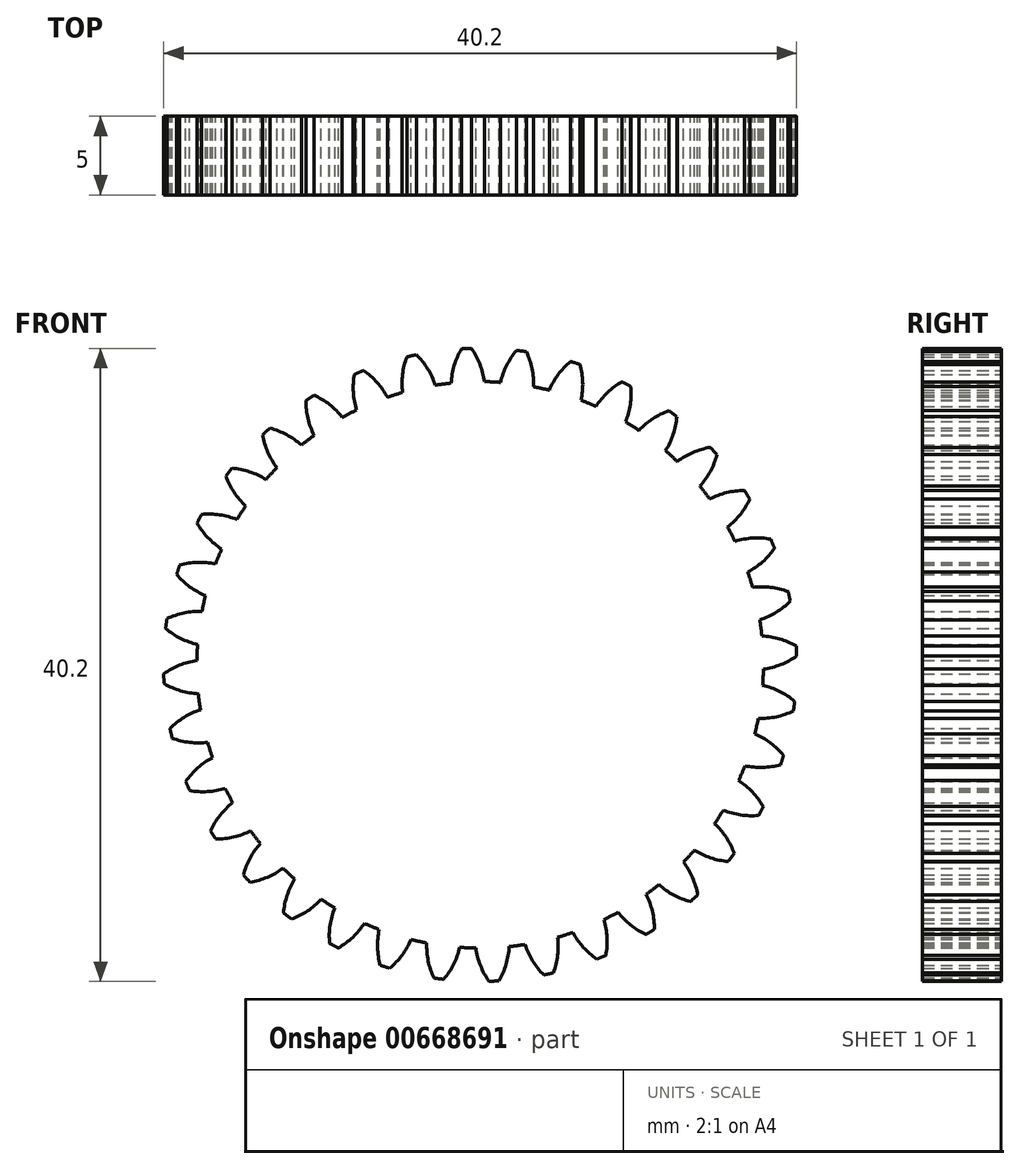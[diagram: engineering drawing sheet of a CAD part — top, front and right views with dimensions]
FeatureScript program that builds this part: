
annotation { "Feature Type Name" : "Feature", "Feature Type Description" : "" }
export const myFeature = defineFeature(function(context is Context, id is Id, definition is map)
    precondition{}
    {
        {
            var Q0;
            Q0=qCreatedBy(makeId("Front.planeOp"),FACE);
            var sketch = newSketch(context, id + "F0", { "sketchPlane" : qUnion([Q0])});
            skLineSegment(sketch, "E0", {"start": v(0, 0) * mm, "end": v(-1.18, 26.95) * mm, "construction": true});
            skArc(sketch, "E1.trimOffspring", {"start": v(0.27, 17.99) * mm, "mid": v(-0.02, 19.1) * mm, "end": v(-0.56, 20.1) * mm});
            skArc(sketch, "E2", {"start": v(-0.56, 20.1) * mm, "mid": v(-0.72, 20.1) * mm, "end": v(-0.88, 20.09) * mm});
            skArc(sketch, "E3.MirrorCS", {"start": v(-1.2, 20.07) * mm, "mid": v(-1.03, 20.08) * mm, "end": v(-0.88, 20.09) * mm});
            skArc(sketch, "E4.MirrorCS", {"start": v(-1.84, 17.9) * mm, "mid": v(-1.65, 19.02) * mm, "end": v(-1.2, 20.07) * mm});
            skArc(sketch, "E5.1.0", {"start": v(-2.85, 17.76) * mm, "mid": v(-3.33, 18.8) * mm, "end": v(-4.05, 19.7) * mm});
            skArc(sketch, "E5.1.1", {"start": v(-4.05, 19.7) * mm, "mid": v(-4.2, 19.66) * mm, "end": v(-4.35, 19.63) * mm});
            skArc(sketch, "E5.1.2", {"start": v(-4.92, 17.3) * mm, "mid": v(-4.93, 18.45) * mm, "end": v(-4.66, 19.56) * mm});
            skArc(sketch, "E5.1.3", {"start": v(-4.66, 19.56) * mm, "mid": v(-4.5, 19.6) * mm, "end": v(-4.35, 19.63) * mm});
            skArc(sketch, "E5.2.0", {"start": v(-5.9, 17) * mm, "mid": v(-6.55, 17.94) * mm, "end": v(-7.4, 18.7) * mm});
            skArc(sketch, "E5.2.1", {"start": v(-7.4, 18.7) * mm, "mid": v(-7.55, 18.64) * mm, "end": v(-7.7, 18.58) * mm});
            skArc(sketch, "E5.2.2", {"start": v(-7.85, 16.19) * mm, "mid": v(-8.05, 17.31) * mm, "end": v(-7.98, 18.46) * mm});
            skArc(sketch, "E5.2.3", {"start": v(-7.98, 18.46) * mm, "mid": v(-7.84, 18.52) * mm, "end": v(-7.7, 18.58) * mm});
            skArc(sketch, "E5.3.0", {"start": v(-8.76, 15.71) * mm, "mid": v(-9.56, 16.53) * mm, "end": v(-10.54, 17.13) * mm});
            skArc(sketch, "E5.3.1", {"start": v(-10.54, 17.13) * mm, "mid": v(-10.67, 17.04) * mm, "end": v(-10.8, 16.96) * mm});
            skArc(sketch, "E5.3.2", {"start": v(-10.54, 14.58) * mm, "mid": v(-10.94, 15.65) * mm, "end": v(-11.07, 16.79) * mm});
            skArc(sketch, "E5.3.3", {"start": v(-11.07, 16.79) * mm, "mid": v(-10.94, 16.87) * mm, "end": v(-10.8, 16.96) * mm});
            skArc(sketch, "E5.4.0", {"start": v(-11.35, 13.96) * mm, "mid": v(-12.29, 14.62) * mm, "end": v(-13.35, 15.04) * mm});
            skArc(sketch, "E5.4.1", {"start": v(-13.35, 15.04) * mm, "mid": v(-13.47, 14.93) * mm, "end": v(-13.58, 14.83) * mm});
            skArc(sketch, "E5.4.2", {"start": v(-12.91, 12.53) * mm, "mid": v(-13.49, 13.51) * mm, "end": v(-13.81, 14.61) * mm});
            skArc(sketch, "E5.4.3", {"start": v(-13.81, 14.61) * mm, "mid": v(-13.7, 14.72) * mm, "end": v(-13.58, 14.83) * mm});
            skArc(sketch, "E5.5.0", {"start": v(-13.6, 11.77) * mm, "mid": v(-14.64, 12.26) * mm, "end": v(-15.76, 12.49) * mm});
            skArc(sketch, "E5.5.1", {"start": v(-15.76, 12.49) * mm, "mid": v(-15.86, 12.37) * mm, "end": v(-15.95, 12.24) * mm});
            skArc(sketch, "E5.5.2", {"start": v(-14.9, 10.1) * mm, "mid": v(-15.63, 10.97) * mm, "end": v(-16.14, 12) * mm});
            skArc(sketch, "E5.5.3", {"start": v(-16.14, 12) * mm, "mid": v(-16.05, 12.12) * mm, "end": v(-15.95, 12.24) * mm});
            skArc(sketch, "E5.6.0", {"start": v(-15.44, 9.23) * mm, "mid": v(-16.55, 9.53) * mm, "end": v(-17.69, 9.56) * mm});
            skArc(sketch, "E5.6.1", {"start": v(-17.69, 9.56) * mm, "mid": v(-17.76, 9.42) * mm, "end": v(-17.84, 9.28) * mm});
            skArc(sketch, "E5.6.2", {"start": v(-16.42, 7.35) * mm, "mid": v(-17.3, 8.09) * mm, "end": v(-17.98, 9) * mm});
            skArc(sketch, "E5.6.3", {"start": v(-17.98, 9) * mm, "mid": v(-17.9, 9.15) * mm, "end": v(-17.84, 9.28) * mm});
            skArc(sketch, "E5.7.0", {"start": v(-16.8, 6.4) * mm, "mid": v(-17.95, 6.51) * mm, "end": v(-19.08, 6.34) * mm});
            skArc(sketch, "E5.7.1", {"start": v(-19.08, 6.34) * mm, "mid": v(-19.13, 6.2) * mm, "end": v(-19.18, 6.05) * mm});
            skArc(sketch, "E5.7.2", {"start": v(-17.45, 4.4) * mm, "mid": v(-18.44, 4.96) * mm, "end": v(-19.27, 5.75) * mm});
            skArc(sketch, "E5.7.3", {"start": v(-19.27, 5.75) * mm, "mid": v(-19.22, 5.9) * mm, "end": v(-19.18, 6.05) * mm});
            skArc(sketch, "E5.8.0", {"start": v(-17.67, 3.4) * mm, "mid": v(-18.8, 3.3) * mm, "end": v(-19.9, 2.94) * mm});
            skArc(sketch, "E5.8.1", {"start": v(-19.9, 2.94) * mm, "mid": v(-19.92, 2.78) * mm, "end": v(-19.94, 2.62) * mm});
            skArc(sketch, "E5.8.2", {"start": v(-17.94, 1.3) * mm, "mid": v(-19.02, 1.68) * mm, "end": v(-19.97, 2.31) * mm});
            skArc(sketch, "E5.8.3", {"start": v(-19.97, 2.31) * mm, "mid": v(-19.96, 2.47) * mm, "end": v(-19.94, 2.62) * mm});
            skArc(sketch, "E5.9.0", {"start": v(-17.99, 0.27) * mm, "mid": v(-19.1, -0.02) * mm, "end": v(-20.1, -0.56) * mm});
            skArc(sketch, "E5.9.1", {"start": v(-20.1, -0.56) * mm, "mid": v(-20.1, -0.72) * mm, "end": v(-20.09, -0.88) * mm});
            skArc(sketch, "E5.9.2", {"start": v(-17.9, -1.84) * mm, "mid": v(-19.02, -1.65) * mm, "end": v(-20.07, -1.2) * mm});
            skArc(sketch, "E5.9.3", {"start": v(-20.07, -1.2) * mm, "mid": v(-20.08, -1.03) * mm, "end": v(-20.09, -0.88) * mm});
            skArc(sketch, "E5.10.0", {"start": v(-17.76, -2.85) * mm, "mid": v(-18.8, -3.33) * mm, "end": v(-19.7, -4.05) * mm});
            skArc(sketch, "E5.10.1", {"start": v(-19.7, -4.05) * mm, "mid": v(-19.66, -4.2) * mm, "end": v(-19.63, -4.35) * mm});
            skArc(sketch, "E5.10.2", {"start": v(-17.3, -4.92) * mm, "mid": v(-18.45, -4.93) * mm, "end": v(-19.56, -4.66) * mm});
            skArc(sketch, "E5.10.3", {"start": v(-19.56, -4.66) * mm, "mid": v(-19.6, -4.5) * mm, "end": v(-19.63, -4.35) * mm});
            skArc(sketch, "E5.11.0", {"start": v(-17, -5.9) * mm, "mid": v(-17.94, -6.55) * mm, "end": v(-18.7, -7.4) * mm});
            skArc(sketch, "E5.11.1", {"start": v(-18.7, -7.4) * mm, "mid": v(-18.64, -7.55) * mm, "end": v(-18.58, -7.7) * mm});
            skArc(sketch, "E5.11.2", {"start": v(-16.19, -7.85) * mm, "mid": v(-17.31, -8.05) * mm, "end": v(-18.46, -7.98) * mm});
            skArc(sketch, "E5.11.3", {"start": v(-18.46, -7.98) * mm, "mid": v(-18.52, -7.84) * mm, "end": v(-18.58, -7.7) * mm});
            skArc(sketch, "E5.12.0", {"start": v(-15.71, -8.76) * mm, "mid": v(-16.53, -9.56) * mm, "end": v(-17.13, -10.54) * mm});
            skArc(sketch, "E5.12.1", {"start": v(-17.13, -10.54) * mm, "mid": v(-17.04, -10.67) * mm, "end": v(-16.96, -10.8) * mm});
            skArc(sketch, "E5.12.2", {"start": v(-14.58, -10.54) * mm, "mid": v(-15.65, -10.94) * mm, "end": v(-16.79, -11.07) * mm});
            skArc(sketch, "E5.12.3", {"start": v(-16.79, -11.07) * mm, "mid": v(-16.87, -10.94) * mm, "end": v(-16.96, -10.8) * mm});
            skArc(sketch, "E5.13.0", {"start": v(-13.96, -11.35) * mm, "mid": v(-14.62, -12.29) * mm, "end": v(-15.04, -13.35) * mm});
            skArc(sketch, "E5.13.1", {"start": v(-15.04, -13.35) * mm, "mid": v(-14.93, -13.47) * mm, "end": v(-14.83, -13.58) * mm});
            skArc(sketch, "E5.13.2", {"start": v(-12.53, -12.91) * mm, "mid": v(-13.51, -13.49) * mm, "end": v(-14.61, -13.81) * mm});
            skArc(sketch, "E5.13.3", {"start": v(-14.61, -13.81) * mm, "mid": v(-14.72, -13.7) * mm, "end": v(-14.83, -13.58) * mm});
            skArc(sketch, "E5.14.0", {"start": v(-11.77, -13.6) * mm, "mid": v(-12.26, -14.64) * mm, "end": v(-12.49, -15.76) * mm});
            skArc(sketch, "E5.14.1", {"start": v(-12.49, -15.76) * mm, "mid": v(-12.37, -15.86) * mm, "end": v(-12.24, -15.95) * mm});
            skArc(sketch, "E5.14.2", {"start": v(-10.1, -14.9) * mm, "mid": v(-10.97, -15.63) * mm, "end": v(-12, -16.14) * mm});
            skArc(sketch, "E5.14.3", {"start": v(-12, -16.14) * mm, "mid": v(-12.12, -16.05) * mm, "end": v(-12.24, -15.95) * mm});
            skArc(sketch, "E5.15.0", {"start": v(-9.23, -15.44) * mm, "mid": v(-9.53, -16.55) * mm, "end": v(-9.56, -17.69) * mm});
            skArc(sketch, "E5.15.1", {"start": v(-9.56, -17.69) * mm, "mid": v(-9.42, -17.76) * mm, "end": v(-9.28, -17.84) * mm});
            skArc(sketch, "E5.15.2", {"start": v(-7.35, -16.42) * mm, "mid": v(-8.09, -17.3) * mm, "end": v(-9, -17.98) * mm});
            skArc(sketch, "E5.15.3", {"start": v(-9, -17.98) * mm, "mid": v(-9.15, -17.9) * mm, "end": v(-9.28, -17.84) * mm});
            skArc(sketch, "E5.16.0", {"start": v(-6.4, -16.8) * mm, "mid": v(-6.51, -17.95) * mm, "end": v(-6.34, -19.08) * mm});
            skArc(sketch, "E5.16.1", {"start": v(-6.34, -19.08) * mm, "mid": v(-6.2, -19.13) * mm, "end": v(-6.05, -19.18) * mm});
            skArc(sketch, "E5.16.2", {"start": v(-4.4, -17.45) * mm, "mid": v(-4.96, -18.44) * mm, "end": v(-5.75, -19.27) * mm});
            skArc(sketch, "E5.16.3", {"start": v(-5.75, -19.27) * mm, "mid": v(-5.9, -19.22) * mm, "end": v(-6.05, -19.18) * mm});
            skArc(sketch, "E5.17.0", {"start": v(-3.4, -17.67) * mm, "mid": v(-3.3, -18.8) * mm, "end": v(-2.94, -19.9) * mm});
            skArc(sketch, "E5.17.1", {"start": v(-2.94, -19.9) * mm, "mid": v(-2.78, -19.92) * mm, "end": v(-2.62, -19.94) * mm});
            skArc(sketch, "E5.17.2", {"start": v(-1.3, -17.94) * mm, "mid": v(-1.68, -19.02) * mm, "end": v(-2.31, -19.97) * mm});
            skArc(sketch, "E5.17.3", {"start": v(-2.31, -19.97) * mm, "mid": v(-2.47, -19.96) * mm, "end": v(-2.62, -19.94) * mm});
            skArc(sketch, "E5.18.0", {"start": v(-0.27, -17.99) * mm, "mid": v(0.02, -19.1) * mm, "end": v(0.56, -20.1) * mm});
            skArc(sketch, "E5.18.1", {"start": v(0.56, -20.1) * mm, "mid": v(0.72, -20.1) * mm, "end": v(0.88, -20.09) * mm});
            skArc(sketch, "E5.18.2", {"start": v(1.84, -17.9) * mm, "mid": v(1.65, -19.02) * mm, "end": v(1.2, -20.07) * mm});
            skArc(sketch, "E5.18.3", {"start": v(1.2, -20.07) * mm, "mid": v(1.03, -20.08) * mm, "end": v(0.88, -20.09) * mm});
            skArc(sketch, "E5.19.0", {"start": v(2.85, -17.76) * mm, "mid": v(3.33, -18.8) * mm, "end": v(4.05, -19.7) * mm});
            skArc(sketch, "E5.19.1", {"start": v(4.05, -19.7) * mm, "mid": v(4.2, -19.66) * mm, "end": v(4.35, -19.63) * mm});
            skArc(sketch, "E5.19.2", {"start": v(4.92, -17.3) * mm, "mid": v(4.93, -18.45) * mm, "end": v(4.66, -19.56) * mm});
            skArc(sketch, "E5.19.3", {"start": v(4.66, -19.56) * mm, "mid": v(4.5, -19.6) * mm, "end": v(4.35, -19.63) * mm});
            skArc(sketch, "E5.20.0", {"start": v(5.9, -17) * mm, "mid": v(6.55, -17.94) * mm, "end": v(7.4, -18.7) * mm});
            skArc(sketch, "E5.20.1", {"start": v(7.4, -18.7) * mm, "mid": v(7.55, -18.64) * mm, "end": v(7.7, -18.58) * mm});
            skArc(sketch, "E5.20.2", {"start": v(7.85, -16.19) * mm, "mid": v(8.05, -17.31) * mm, "end": v(7.98, -18.46) * mm});
            skArc(sketch, "E5.20.3", {"start": v(7.98, -18.46) * mm, "mid": v(7.84, -18.52) * mm, "end": v(7.7, -18.58) * mm});
            skArc(sketch, "E5.21.0", {"start": v(8.76, -15.71) * mm, "mid": v(9.56, -16.53) * mm, "end": v(10.54, -17.13) * mm});
            skArc(sketch, "E5.21.1", {"start": v(10.54, -17.13) * mm, "mid": v(10.67, -17.04) * mm, "end": v(10.8, -16.96) * mm});
            skArc(sketch, "E5.21.2", {"start": v(10.54, -14.58) * mm, "mid": v(10.94, -15.65) * mm, "end": v(11.07, -16.79) * mm});
            skArc(sketch, "E5.21.3", {"start": v(11.07, -16.79) * mm, "mid": v(10.94, -16.87) * mm, "end": v(10.8, -16.96) * mm});
            skArc(sketch, "E5.22.0", {"start": v(11.35, -13.96) * mm, "mid": v(12.29, -14.62) * mm, "end": v(13.35, -15.04) * mm});
            skArc(sketch, "E5.22.1", {"start": v(13.35, -15.04) * mm, "mid": v(13.47, -14.93) * mm, "end": v(13.58, -14.83) * mm});
            skArc(sketch, "E5.22.2", {"start": v(12.91, -12.53) * mm, "mid": v(13.49, -13.51) * mm, "end": v(13.81, -14.61) * mm});
            skArc(sketch, "E5.22.3", {"start": v(13.81, -14.61) * mm, "mid": v(13.7, -14.72) * mm, "end": v(13.58, -14.83) * mm});
            skArc(sketch, "E5.23.0", {"start": v(13.6, -11.77) * mm, "mid": v(14.64, -12.26) * mm, "end": v(15.76, -12.49) * mm});
            skArc(sketch, "E5.23.1", {"start": v(15.76, -12.49) * mm, "mid": v(15.86, -12.37) * mm, "end": v(15.95, -12.24) * mm});
            skArc(sketch, "E5.23.2", {"start": v(14.9, -10.1) * mm, "mid": v(15.63, -10.97) * mm, "end": v(16.14, -12) * mm});
            skArc(sketch, "E5.23.3", {"start": v(16.14, -12) * mm, "mid": v(16.05, -12.12) * mm, "end": v(15.95, -12.24) * mm});
            skArc(sketch, "E5.24.0", {"start": v(15.44, -9.23) * mm, "mid": v(16.55, -9.53) * mm, "end": v(17.69, -9.56) * mm});
            skArc(sketch, "E5.24.1", {"start": v(17.69, -9.56) * mm, "mid": v(17.76, -9.42) * mm, "end": v(17.84, -9.28) * mm});
            skArc(sketch, "E5.24.2", {"start": v(16.42, -7.35) * mm, "mid": v(17.3, -8.09) * mm, "end": v(17.98, -9) * mm});
            skArc(sketch, "E5.24.3", {"start": v(17.98, -9) * mm, "mid": v(17.9, -9.15) * mm, "end": v(17.84, -9.28) * mm});
            skArc(sketch, "E5.25.0", {"start": v(16.8, -6.4) * mm, "mid": v(17.95, -6.51) * mm, "end": v(19.08, -6.34) * mm});
            skArc(sketch, "E5.25.1", {"start": v(19.08, -6.34) * mm, "mid": v(19.13, -6.2) * mm, "end": v(19.18, -6.05) * mm});
            skArc(sketch, "E5.25.2", {"start": v(17.45, -4.4) * mm, "mid": v(18.44, -4.96) * mm, "end": v(19.27, -5.75) * mm});
            skArc(sketch, "E5.25.3", {"start": v(19.27, -5.75) * mm, "mid": v(19.22, -5.9) * mm, "end": v(19.18, -6.05) * mm});
            skArc(sketch, "E5.26.0", {"start": v(17.67, -3.4) * mm, "mid": v(18.8, -3.3) * mm, "end": v(19.9, -2.94) * mm});
            skArc(sketch, "E5.26.1", {"start": v(19.9, -2.94) * mm, "mid": v(19.92, -2.78) * mm, "end": v(19.94, -2.62) * mm});
            skArc(sketch, "E5.26.2", {"start": v(17.94, -1.3) * mm, "mid": v(19.02, -1.68) * mm, "end": v(19.97, -2.31) * mm});
            skArc(sketch, "E5.26.3", {"start": v(19.97, -2.31) * mm, "mid": v(19.96, -2.47) * mm, "end": v(19.94, -2.62) * mm});
            skArc(sketch, "E5.27.0", {"start": v(17.99, -0.27) * mm, "mid": v(19.1, 0.02) * mm, "end": v(20.1, 0.56) * mm});
            skArc(sketch, "E5.27.1", {"start": v(20.1, 0.56) * mm, "mid": v(20.1, 0.72) * mm, "end": v(20.09, 0.88) * mm});
            skArc(sketch, "E5.27.2", {"start": v(17.9, 1.84) * mm, "mid": v(19.02, 1.65) * mm, "end": v(20.07, 1.2) * mm});
            skArc(sketch, "E5.27.3", {"start": v(20.07, 1.2) * mm, "mid": v(20.08, 1.03) * mm, "end": v(20.09, 0.88) * mm});
            skArc(sketch, "E5.28.0", {"start": v(17.76, 2.85) * mm, "mid": v(18.8, 3.33) * mm, "end": v(19.7, 4.05) * mm});
            skArc(sketch, "E5.28.1", {"start": v(19.7, 4.05) * mm, "mid": v(19.66, 4.2) * mm, "end": v(19.63, 4.35) * mm});
            skArc(sketch, "E5.28.2", {"start": v(17.3, 4.92) * mm, "mid": v(18.45, 4.93) * mm, "end": v(19.56, 4.66) * mm});
            skArc(sketch, "E5.28.3", {"start": v(19.56, 4.66) * mm, "mid": v(19.6, 4.5) * mm, "end": v(19.63, 4.35) * mm});
            skArc(sketch, "E5.29.0", {"start": v(17, 5.9) * mm, "mid": v(17.94, 6.55) * mm, "end": v(18.7, 7.4) * mm});
            skArc(sketch, "E5.29.1", {"start": v(18.7, 7.4) * mm, "mid": v(18.64, 7.55) * mm, "end": v(18.58, 7.7) * mm});
            skArc(sketch, "E5.29.2", {"start": v(16.19, 7.85) * mm, "mid": v(17.31, 8.05) * mm, "end": v(18.46, 7.98) * mm});
            skArc(sketch, "E5.29.3", {"start": v(18.46, 7.98) * mm, "mid": v(18.52, 7.84) * mm, "end": v(18.58, 7.7) * mm});
            skArc(sketch, "E5.30.0", {"start": v(15.71, 8.76) * mm, "mid": v(16.53, 9.56) * mm, "end": v(17.13, 10.54) * mm});
            skArc(sketch, "E5.30.1", {"start": v(17.13, 10.54) * mm, "mid": v(17.04, 10.67) * mm, "end": v(16.96, 10.8) * mm});
            skArc(sketch, "E5.30.2", {"start": v(14.58, 10.54) * mm, "mid": v(15.65, 10.94) * mm, "end": v(16.79, 11.07) * mm});
            skArc(sketch, "E5.30.3", {"start": v(16.79, 11.07) * mm, "mid": v(16.87, 10.94) * mm, "end": v(16.96, 10.8) * mm});
            skArc(sketch, "E5.31.0", {"start": v(13.96, 11.35) * mm, "mid": v(14.62, 12.29) * mm, "end": v(15.04, 13.35) * mm});
            skArc(sketch, "E5.31.1", {"start": v(15.04, 13.35) * mm, "mid": v(14.93, 13.47) * mm, "end": v(14.83, 13.58) * mm});
            skArc(sketch, "E5.31.2", {"start": v(12.53, 12.91) * mm, "mid": v(13.51, 13.49) * mm, "end": v(14.61, 13.81) * mm});
            skArc(sketch, "E5.31.3", {"start": v(14.61, 13.81) * mm, "mid": v(14.72, 13.7) * mm, "end": v(14.83, 13.58) * mm});
            skArc(sketch, "E5.32.0", {"start": v(11.77, 13.6) * mm, "mid": v(12.26, 14.64) * mm, "end": v(12.49, 15.76) * mm});
            skArc(sketch, "E5.32.1", {"start": v(12.49, 15.76) * mm, "mid": v(12.37, 15.86) * mm, "end": v(12.24, 15.95) * mm});
            skArc(sketch, "E5.32.2", {"start": v(10.1, 14.9) * mm, "mid": v(10.97, 15.63) * mm, "end": v(12, 16.14) * mm});
            skArc(sketch, "E5.32.3", {"start": v(12, 16.14) * mm, "mid": v(12.12, 16.05) * mm, "end": v(12.24, 15.95) * mm});
            skArc(sketch, "E5.33.0", {"start": v(9.23, 15.44) * mm, "mid": v(9.53, 16.55) * mm, "end": v(9.56, 17.69) * mm});
            skArc(sketch, "E5.33.1", {"start": v(9.56, 17.69) * mm, "mid": v(9.42, 17.76) * mm, "end": v(9.28, 17.84) * mm});
            skArc(sketch, "E5.33.2", {"start": v(7.35, 16.42) * mm, "mid": v(8.09, 17.3) * mm, "end": v(9, 17.98) * mm});
            skArc(sketch, "E5.33.3", {"start": v(9, 17.98) * mm, "mid": v(9.15, 17.9) * mm, "end": v(9.28, 17.84) * mm});
            skArc(sketch, "E5.34.0", {"start": v(6.4, 16.8) * mm, "mid": v(6.51, 17.95) * mm, "end": v(6.34, 19.08) * mm});
            skArc(sketch, "E5.34.1", {"start": v(6.34, 19.08) * mm, "mid": v(6.2, 19.13) * mm, "end": v(6.05, 19.18) * mm});
            skArc(sketch, "E5.34.2", {"start": v(4.4, 17.45) * mm, "mid": v(4.96, 18.44) * mm, "end": v(5.75, 19.27) * mm});
            skArc(sketch, "E5.34.3", {"start": v(5.75, 19.27) * mm, "mid": v(5.9, 19.22) * mm, "end": v(6.05, 19.18) * mm});
            skArc(sketch, "E5.35.0", {"start": v(3.4, 17.67) * mm, "mid": v(3.3, 18.8) * mm, "end": v(2.94, 19.9) * mm});
            skArc(sketch, "E5.35.1", {"start": v(2.94, 19.9) * mm, "mid": v(2.78, 19.92) * mm, "end": v(2.62, 19.94) * mm});
            skArc(sketch, "E5.35.2", {"start": v(1.3, 17.94) * mm, "mid": v(1.68, 19.02) * mm, "end": v(2.31, 19.97) * mm});
            skArc(sketch, "E5.35.3", {"start": v(2.31, 19.97) * mm, "mid": v(2.47, 19.96) * mm, "end": v(2.62, 19.94) * mm});
            skArc(sketch, "E6", {"start": v(-4.92, 17.3) * mm, "mid": v(-5.4, 17.16) * mm, "end": v(-5.9, 17) * mm});
            skArc(sketch, "E7.trimOffspring", {"start": v(-1.84, 17.9) * mm, "mid": v(-2.35, 17.84) * mm, "end": v(-2.85, 17.76) * mm});
            skArc(sketch, "E8.trimOffspring", {"start": v(1.3, 17.94) * mm, "mid": v(0.78, 17.97) * mm, "end": v(0.27, 17.99) * mm});
            skArc(sketch, "E9.trimOffspring", {"start": v(4.4, 17.45) * mm, "mid": v(3.9, 17.56) * mm, "end": v(3.4, 17.67) * mm});
            skArc(sketch, "E10.trimOffspring", {"start": v(7.35, 16.42) * mm, "mid": v(6.88, 16.62) * mm, "end": v(6.4, 16.8) * mm});
            skArc(sketch, "E11.trimOffspring", {"start": v(10.1, 14.9) * mm, "mid": v(9.67, 15.17) * mm, "end": v(9.23, 15.44) * mm});
            skArc(sketch, "E12.trimOffspring", {"start": v(12.53, 12.91) * mm, "mid": v(12.15, 13.26) * mm, "end": v(11.77, 13.6) * mm});
            skArc(sketch, "E13.trimOffspring", {"start": v(16.19, 7.85) * mm, "mid": v(15.96, 8.3) * mm, "end": v(15.71, 8.76) * mm});
            skArc(sketch, "E14.trimOffspring", {"start": v(17.3, 4.92) * mm, "mid": v(17.16, 5.4) * mm, "end": v(17, 5.9) * mm});
            skArc(sketch, "E15.trimOffspring", {"start": v(14.58, 10.54) * mm, "mid": v(14.27, 10.95) * mm, "end": v(13.96, 11.35) * mm});
            skArc(sketch, "E16.trimOffspring", {"start": v(17.9, 1.84) * mm, "mid": v(17.84, 2.35) * mm, "end": v(17.76, 2.85) * mm});
            skArc(sketch, "E17.trimOffspring", {"start": v(17.94, -1.3) * mm, "mid": v(17.97, -0.78) * mm, "end": v(17.99, -0.27) * mm});
            skArc(sketch, "E18.trimOffspring", {"start": v(17.45, -4.4) * mm, "mid": v(17.56, -3.9) * mm, "end": v(17.67, -3.4) * mm});
            skArc(sketch, "E19.trimOffspring", {"start": v(16.42, -7.35) * mm, "mid": v(16.62, -6.88) * mm, "end": v(16.8, -6.4) * mm});
            skArc(sketch, "E20.trimOffspring", {"start": v(14.9, -10.1) * mm, "mid": v(15.17, -9.67) * mm, "end": v(15.44, -9.23) * mm});
            skArc(sketch, "E21.trimOffspring", {"start": v(12.91, -12.53) * mm, "mid": v(13.26, -12.15) * mm, "end": v(13.6, -11.77) * mm});
            skArc(sketch, "E22.trimOffspring", {"start": v(10.54, -14.58) * mm, "mid": v(10.95, -14.27) * mm, "end": v(11.35, -13.96) * mm});
            skArc(sketch, "E23.trimOffspring", {"start": v(7.85, -16.19) * mm, "mid": v(8.3, -15.96) * mm, "end": v(8.76, -15.71) * mm});
            skArc(sketch, "E24.trimOffspring", {"start": v(4.92, -17.3) * mm, "mid": v(5.4, -17.16) * mm, "end": v(5.9, -17) * mm});
            skArc(sketch, "E25.trimOffspring", {"start": v(1.84, -17.9) * mm, "mid": v(2.35, -17.84) * mm, "end": v(2.85, -17.76) * mm});
            skArc(sketch, "E26.trimOffspring", {"start": v(-1.3, -17.94) * mm, "mid": v(-0.78, -17.97) * mm, "end": v(-0.27, -17.99) * mm});
            skArc(sketch, "E27.trimOffspring", {"start": v(-4.4, -17.45) * mm, "mid": v(-3.9, -17.56) * mm, "end": v(-3.4, -17.67) * mm});
            skArc(sketch, "E28.trimOffspring", {"start": v(-7.35, -16.42) * mm, "mid": v(-6.88, -16.62) * mm, "end": v(-6.4, -16.8) * mm});
            skArc(sketch, "E29.trimOffspring", {"start": v(-10.1, -14.9) * mm, "mid": v(-9.67, -15.17) * mm, "end": v(-9.23, -15.44) * mm});
            skArc(sketch, "E30.trimOffspring", {"start": v(-12.53, -12.91) * mm, "mid": v(-12.15, -13.26) * mm, "end": v(-11.77, -13.6) * mm});
            skArc(sketch, "E31.trimOffspring", {"start": v(-14.58, -10.54) * mm, "mid": v(-14.27, -10.95) * mm, "end": v(-13.96, -11.35) * mm});
            skArc(sketch, "E32.trimOffspring", {"start": v(-16.19, -7.85) * mm, "mid": v(-15.96, -8.3) * mm, "end": v(-15.71, -8.76) * mm});
            skArc(sketch, "E33.trimOffspring", {"start": v(-17.3, -4.92) * mm, "mid": v(-17.16, -5.4) * mm, "end": v(-17, -5.9) * mm});
            skArc(sketch, "E34.trimOffspring", {"start": v(-17.9, -1.84) * mm, "mid": v(-17.84, -2.35) * mm, "end": v(-17.76, -2.85) * mm});
            skArc(sketch, "E35.trimOffspring", {"start": v(-17.94, 1.3) * mm, "mid": v(-17.97, 0.78) * mm, "end": v(-17.99, 0.27) * mm});
            skArc(sketch, "E36.trimOffspring", {"start": v(-17.45, 4.4) * mm, "mid": v(-17.56, 3.9) * mm, "end": v(-17.67, 3.4) * mm});
            skArc(sketch, "E37.trimOffspring", {"start": v(-16.42, 7.35) * mm, "mid": v(-16.62, 6.88) * mm, "end": v(-16.8, 6.4) * mm});
            skArc(sketch, "E38.trimOffspring", {"start": v(-14.9, 10.1) * mm, "mid": v(-15.17, 9.67) * mm, "end": v(-15.44, 9.23) * mm});
            skArc(sketch, "E39.trimOffspring", {"start": v(-12.91, 12.53) * mm, "mid": v(-13.26, 12.15) * mm, "end": v(-13.6, 11.77) * mm});
            skArc(sketch, "E40.trimOffspring", {"start": v(-10.54, 14.58) * mm, "mid": v(-10.95, 14.27) * mm, "end": v(-11.35, 13.96) * mm});
            skArc(sketch, "E41.trimOffspring", {"start": v(-7.85, 16.19) * mm, "mid": v(-8.3, 15.96) * mm, "end": v(-8.76, 15.71) * mm});
            skSolve(sketch);
        }
        {
            var Q0;
            Q0=makeQuery(id+"F0.imprint","IMPRINT",FACE,{"disambiguationData":[TD([[makeQuery(id+"F0.imprint","IMPRINT",EDGE,{"derivedFrom":sQuery(id+"F0.wireOp",EDGE,"E1.trimOffspring")}),1.0]])]});
            extrude(context, id + "F1", {"entities" : qUnion([Q0]), "depth" : 5 * mm, "offsetDistance" : 25 * mm});
        }
    });
